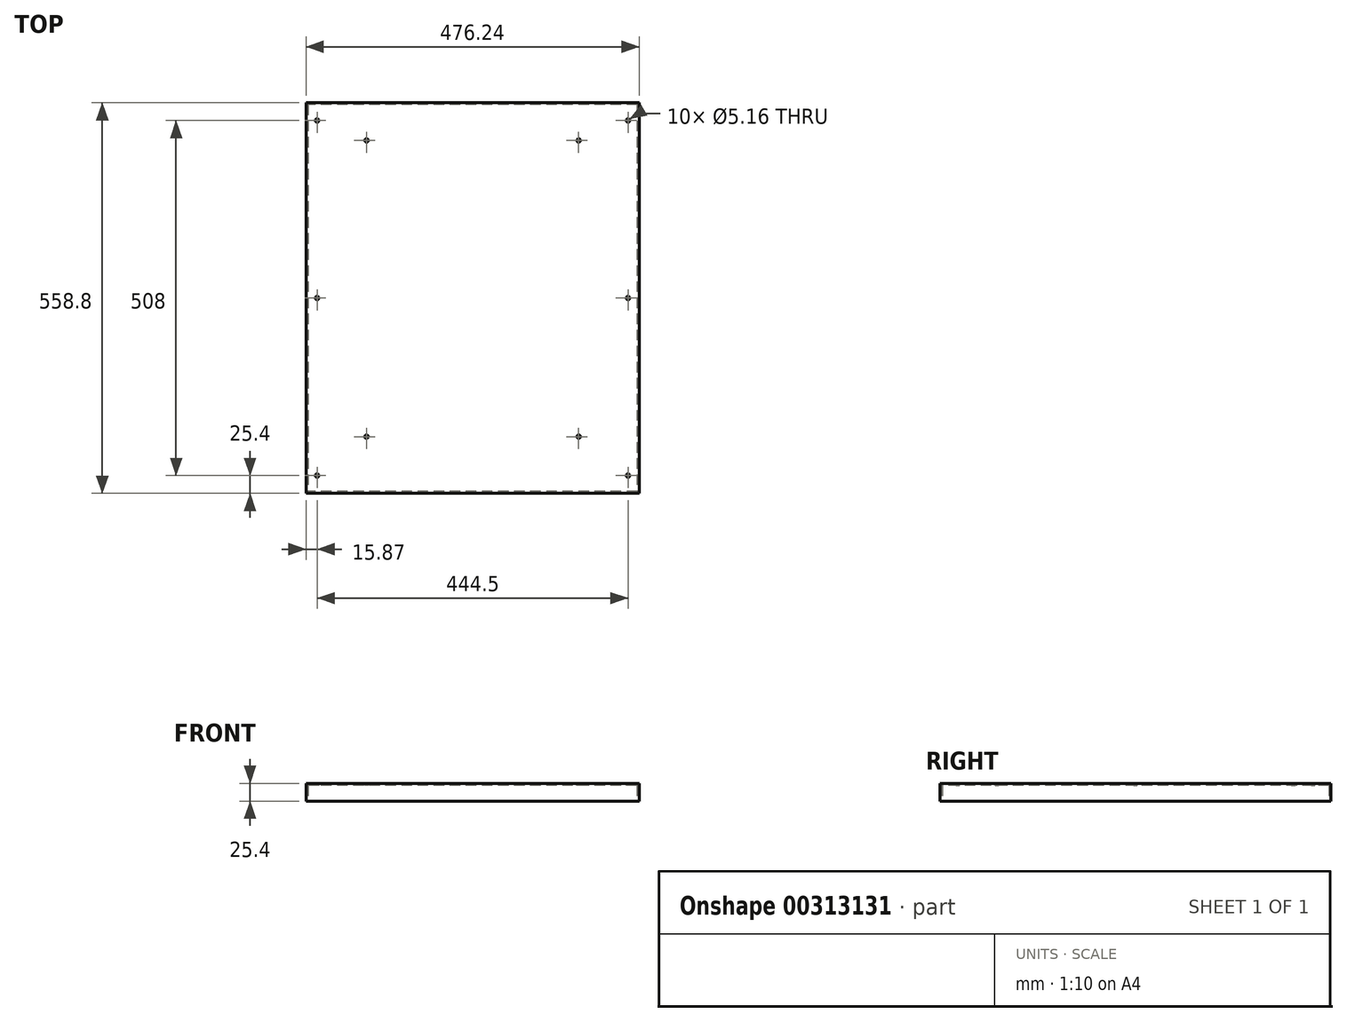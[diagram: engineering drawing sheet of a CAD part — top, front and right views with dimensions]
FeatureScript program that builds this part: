
annotation { "Feature Type Name" : "Feature", "Feature Type Description" : "" }
export const myFeature = defineFeature(function(context is Context, id is Id, definition is map)
    precondition{}
    {
        {
            var Q0;
            Q0=qCreatedBy(makeId("Top.planeOp"),FACE);
            var sketch = newSketch(context, id + "F0", { "sketchPlane" : qUnion([Q0])});
            skLineSegment(sketch, "E0.bottom", {"start": v(238.12, 279.4) * mm, "end": v(-238.13, 279.4) * mm});
            skLineSegment(sketch, "E0.top", {"start": v(238.13, -279.4) * mm, "end": v(-238.12, -279.4) * mm});
            skLineSegment(sketch, "E0.left", {"start": v(238.12, 279.4) * mm, "end": v(238.13, -279.4) * mm});
            skLineSegment(sketch, "E0.right", {"start": v(-238.13, 279.4) * mm, "end": v(-238.12, -279.4) * mm});
            skPoint(sketch, "E0.middle", {"position": v(0, 0) * mm});
            skSolve(sketch);
        }
        {
            var Q0;
            Q0=qSketchRegion(id+"F0",true);
            extrude(context, id + "F1", {"entities" : qUnion([Q0]), "endBound" : BoundingType.SYMMETRIC, "depth" : 25.4 * mm});
        }
        {
            var Q0;
            Q0=makeQuery(id+"F1.opExtrude","CAP_FACE",FACE,{"disambiguationData":[OSD([sQuery(id+"F0.wireOp",EDGE,"E0.bottom"),sQuery(id+"F0.wireOp",EDGE,"E0.top"),sQuery(id+"F0.wireOp",EDGE,"E0.left"),sQuery(id+"F0.wireOp",EDGE,"E0.right")])],"isStart":true});
            shell(context, id + "F2", {"entities" : qUnion([Q0]), "thickness" : 2.75 * mm});
        }
        {
            var Q0;
            Q0=makeQuery(id+"F1.opExtrude","CAP_FACE",FACE,{"disambiguationData":[OSD([sQuery(id+"F0.wireOp",EDGE,"E0.bottom"),sQuery(id+"F0.wireOp",EDGE,"E0.top"),sQuery(id+"F0.wireOp",EDGE,"E0.left"),sQuery(id+"F0.wireOp",EDGE,"E0.right")])],"isStart":false});
            var sketch = newSketch(context, id + "F3", { "sketchPlane" : qUnion([Q0])});
            skCircle(sketch, "E1", {"center": v(-151.6, 225.43) * mm, "radius": 2.58 * mm});
            skCircle(sketch, "E2", {"center": v(151.6, 225.43) * mm, "radius": 2.58 * mm});
            skCircle(sketch, "E3", {"center": v(151.6, -198.44) * mm, "radius": 2.58 * mm});
            skCircle(sketch, "E4", {"center": v(-151.6, -198.44) * mm, "radius": 2.58 * mm});
            skLineSegment(sketch, "E5", {"start": v(-151.6, 225.42) * mm, "end": v(151.6, 225.43) * mm, "construction": true});
            skPoint(sketch, "E6", {"position": v(0, 225.43) * mm});
            skCircle(sketch, "E7", {"center": v(-222.25, -254) * mm, "radius": 2.58 * mm});
            skCircle(sketch, "E8", {"center": v(-222.25, 254) * mm, "radius": 2.58 * mm});
            skCircle(sketch, "E9", {"center": v(222.25, -254) * mm, "radius": 2.58 * mm});
            skCircle(sketch, "E10", {"center": v(222.25, 254) * mm, "radius": 2.58 * mm});
            skPoint(sketch, "E11.centerSnap0", {"position": v(-238.13, 0) * mm});
            skCircle(sketch, "E12", {"center": v(-222.25, 0) * mm, "radius": 2.58 * mm});
            skCircle(sketch, "E13", {"center": v(222.25, 0) * mm, "radius": 2.58 * mm});
            skLineSegment(sketch, "E14", {"start": v(151.6, 225.43) * mm, "end": v(151.6, -198.44) * mm, "construction": true});
            skPoint(sketch, "E15", {"position": v(151.6, 13.5) * mm});
            skSolve(sketch);
        }
        {
            var Q0;
            Q0=qSketchRegion(id+"F3",true);
            extrude(context, id + "F4", {"entities" : qUnion([Q0]), "operationType" : NewBodyOperationType.REMOVE, "endBound" : BoundingType.THROUGH_ALL, "oppositeDirection" : true, "depth" : 25.4 * mm});
        }
    });
